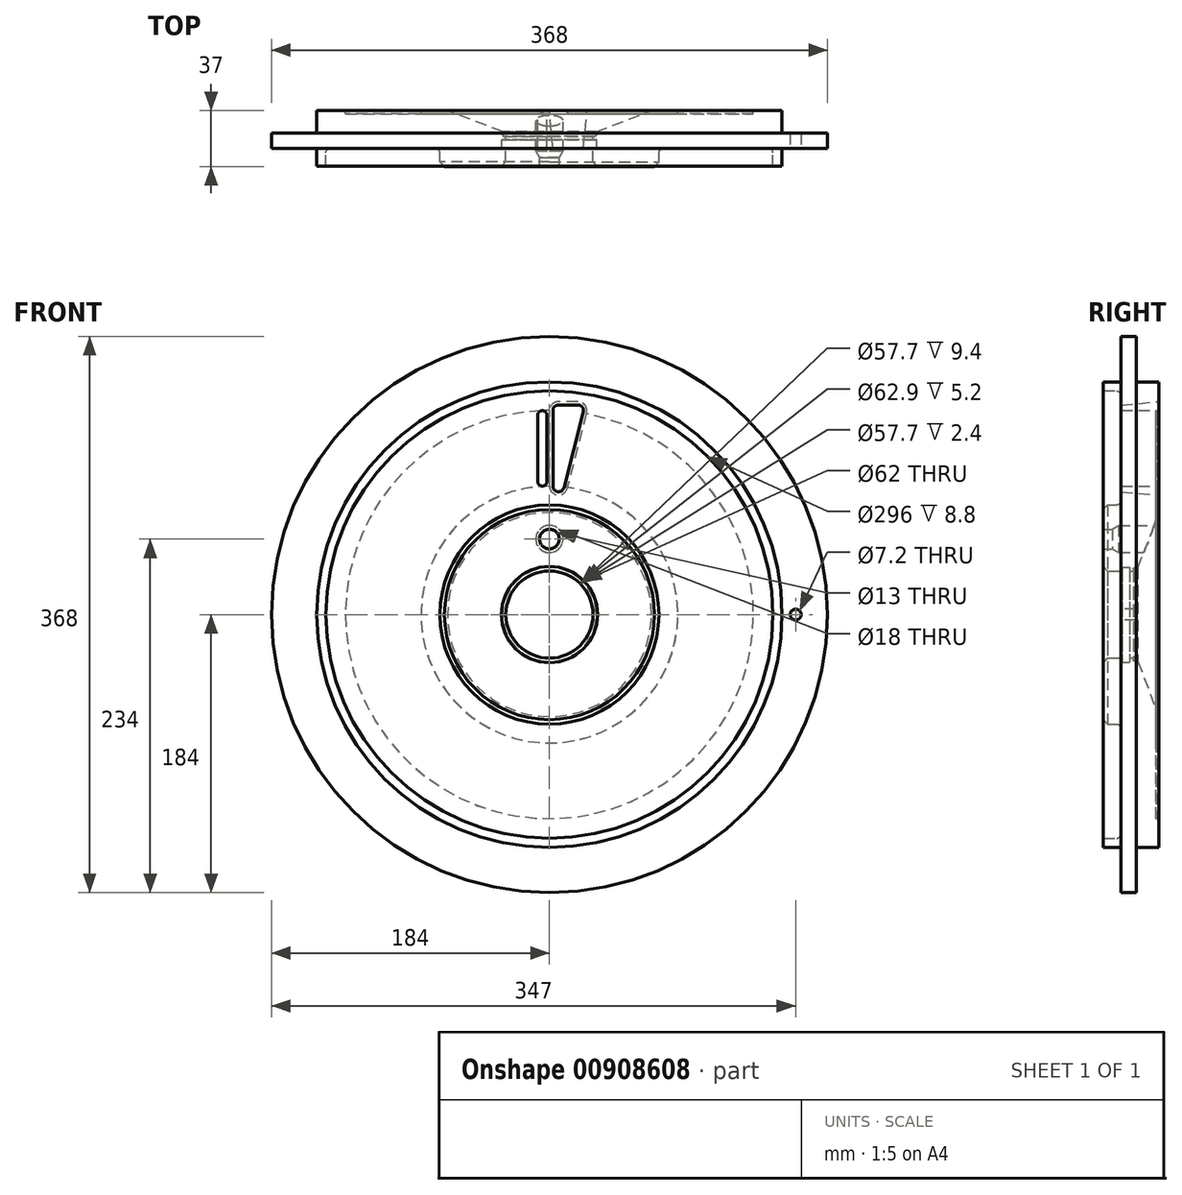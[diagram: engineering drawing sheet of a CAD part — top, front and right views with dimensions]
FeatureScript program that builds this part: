
annotation { "Feature Type Name" : "Feature", "Feature Type Description" : "" }
export const myFeature = defineFeature(function(context is Context, id is Id, definition is map)
    precondition{}
    {
        {
            var Q0;
            Q0=qCreatedBy(makeId("Top.planeOp"),FACE);
            var sketch = newSketch(context, id + "F0", { "sketchPlane" : qUnion([Q0])});
            skLineSegment(sketch, "E0", {"start": v(-72.5, 9) * mm, "end": v(-72.5, 0) * mm});
            skLineSegment(sketch, "E1", {"start": v(-72.5, 0) * mm, "end": v(-28.85, 0) * mm});
            skLineSegment(sketch, "E2", {"start": v(0, 47.35) * mm, "end": v(0, -31.33) * mm, "construction": true});
            skPoint(sketch, "E3.visualSharp", {"position": v(-72.5, 10) * mm});
            skLineSegment(sketch, "E4", {"start": v(-22.07, -0.9) * mm, "end": v(27.18, -0.9) * mm, "construction": true});
            skLineSegment(sketch, "E5", {"start": v(-154, 12) * mm, "end": v(-154, 0.2) * mm});
            skLineSegment(sketch, "E6", {"start": v(-154, 0.2) * mm, "end": v(-148, 0.2) * mm});
            skLineSegment(sketch, "E7", {"start": v(-148, 0.2) * mm, "end": v(-148, 9) * mm});
            skLineSegment(sketch, "E8", {"start": v(-28.85, 20) * mm, "end": v(-30, 20) * mm});
            skPoint(sketch, "E9.visualSharp", {"position": v(-35.7, 20) * mm});
            skLineSegment(sketch, "E10", {"start": v(-28.85, 20) * mm, "end": v(-28.85, 17.6) * mm});
            skLineSegment(sketch, "E11", {"start": v(-28.85, 17.6) * mm, "end": v(-31.45, 17.6) * mm});
            skLineSegment(sketch, "E12", {"start": v(-31.45, 17.6) * mm, "end": v(-31.45, 12.4) * mm});
            skLineSegment(sketch, "E13", {"start": v(-31.45, 12.4) * mm, "end": v(-28.85, 12.4) * mm});
            skLineSegment(sketch, "E14", {"start": v(-28.85, 12.4) * mm, "end": v(-28.85, 0) * mm});
            skLineSegment(sketch, "E15", {"start": v(-154, 12) * mm, "end": v(-184, 12) * mm});
            skLineSegment(sketch, "E16", {"start": v(-154, 37) * mm, "end": v(-67.5, 37) * mm});
            skPoint(sketch, "E17.visualSharp", {"position": v(-35, 23.4) * mm});
            skLineSegment(sketch, "E18", {"start": v(-145, 12) * mm, "end": v(-75.5, 12) * mm});
            skPoint(sketch, "E19.orphan", {"position": v(-148, 11.2) * mm});
            skPoint(sketch, "E20.visualSharp", {"position": v(-148, 12) * mm});
            skArc(sketch, "E20.filletArc", {"start": v(-145, 12) * mm, "mid": v(-147.12, 11.12) * mm, "end": v(-148, 9) * mm});
            skPoint(sketch, "E21.visualSharp", {"position": v(-72.5, 12) * mm});
            skArc(sketch, "E21.filletArc", {"start": v(-72.5, 9) * mm, "mid": v(-73.38, 11.12) * mm, "end": v(-75.5, 12) * mm});
            skLineSegment(sketch, "E22", {"start": v(-184, 12) * mm, "end": v(-184, 22) * mm});
            skLineSegment(sketch, "E23", {"start": v(-184, 22) * mm, "end": v(-154, 22) * mm});
            skLineSegment(sketch, "E24", {"start": v(-154, 22) * mm, "end": v(-154, 37) * mm});
            skLineSegment(sketch, "E25", {"start": v(-31, 23) * mm, "end": v(-67.5, 37) * mm});
            skLineSegment(sketch, "E26", {"start": v(-31, 23) * mm, "end": v(-31, 21) * mm});
            skPoint(sketch, "E27.visualSharp", {"position": v(-31, 20) * mm});
            skArc(sketch, "E27.filletArc", {"start": v(-31, 21) * mm, "mid": v(-30.7, 20.3) * mm, "end": v(-30, 20) * mm});
            skSolve(sketch);
        }
        {
            var Q0;
            Q0=makeQuery(id+"F0.imprint","IMPRINT",FACE,{"disambiguationData":[TD([[makeQuery(id+"F0.imprint","IMPRINT",EDGE,{"derivedFrom":sQuery(id+"F0.wireOp",EDGE,"E0")}),1.0]])]});
            var Q1;
            Q1=sQuery(id+"F0.wireOp",EDGE,"E2");
            revolve(context, id + "F1", {"surfaceOperationType" : NewSurfaceOperationType.NEW, "entities" : qUnion([Q0]), "axis" : qUnion([Q1]), "revolveType" : RevolveType.FULL});
        }
        {
            var Q0;
            Q0=qCreatedBy(makeId("Front.planeOp"),FACE);
            cPlane(context, id + "F2", {"entities" : qUnion([Q0]), "cplaneType" : CPlaneType.OFFSET, "offset" : 38 * mm, "oppositeDirection" : true, "width" : 150 * mm, "height" : 150 * mm});
        }
        {
            var Q0;
            Q0=qCreatedBy(id+"F2.planeOp",FACE);
            var sketch = newSketch(context, id + "F3", { "sketchPlane" : qUnion([Q0])});
            skLineSegment(sketch, "E28", {"start": v(0, 85) * mm, "end": v(0, 135) * mm});
            skLineSegment(sketch, "E29", {"start": v(6, 141) * mm, "end": v(18.84, 141) * mm});
            skLineSegment(sketch, "E30", {"start": v(24.65, 133.5) * mm, "end": v(11.81, 83.5) * mm});
            skPoint(sketch, "E31.visualSharp", {"position": v(26.57, 141) * mm});
            skArc(sketch, "E31.filletArc", {"start": v(24.65, 133.5) * mm, "mid": v(23.58, 138.68) * mm, "end": v(18.84, 141) * mm});
            skPoint(sketch, "E32.visualSharp", {"position": v(0, 37.5) * mm});
            skArc(sketch, "E32.filletArc", {"start": v(0, 85) * mm, "mid": v(5.25, 79.05) * mm, "end": v(11.81, 83.5) * mm});
            skPoint(sketch, "E33.visualSharp", {"position": v(0, 141) * mm});
            skArc(sketch, "E33.filletArc", {"start": v(6, 141) * mm, "mid": v(1.76, 139.24) * mm, "end": v(0, 135) * mm});
            skSolve(sketch);
        }
        {
            var Q0;
            Q0=qCreatedBy(makeId("Front.planeOp"),FACE);
            var sketch = newSketch(context, id + "F4", { "sketchPlane" : qUnion([Q0])});
            skCircle(sketch, "E34", {"center": v(163, 0) * mm, "radius": 3.6 * mm});
            skSolve(sketch);
        }
        {
            var Q0;
            Q0=qSketchRegion(id+"F4",true);
            extrude(context, id + "F5", {"entities" : qUnion([Q0]), "operationType" : NewBodyOperationType.REMOVE, "oppositeDirection" : true, "depth" : 50 * mm, "offsetDistance" : 25 * mm});
        }
        {
            var Q0;
            Q0=qCreatedBy(makeId("Right.planeOp"),FACE);
            var sketch = newSketch(context, id + "F6", { "sketchPlane" : qUnion([Q0])});
            skLineSegment(sketch, "E35", {"start": v(0, 50) * mm, "end": v(51.06, 50) * mm});
            skLineSegment(sketch, "E36", {"start": v(0, 56.5) * mm, "end": v(6, 56.5) * mm});
            skLineSegment(sketch, "E37", {"start": v(6, 56.5) * mm, "end": v(10.33, 59) * mm});
            skLineSegment(sketch, "E38", {"start": v(10.33, 59) * mm, "end": v(51.06, 59) * mm});
            skLineSegment(sketch, "E39", {"start": v(51.06, 59) * mm, "end": v(51.06, 50) * mm});
            skLineSegment(sketch, "E40", {"start": v(0, 50) * mm, "end": v(0, 56.5) * mm});
            skSolve(sketch);
        }
        {
            var Q0;
            Q0=qSketchRegion(id+"F6",true);
            var Q1;
            Q1=sQuery(id+"F6.wireOp",EDGE,"E35");
            revolve(context, id + "F7", {"operationType" : NewBodyOperationType.REMOVE, "surfaceOperationType" : NewSurfaceOperationType.NEW, "entities" : qUnion([Q0]), "axis" : qUnion([Q1]), "revolveType" : RevolveType.FULL, "oppositeDirection" : true});
        }
        {
            var Q0;
            Q0=makeQuery(id+"F1.opRevolve","SWEPT_EDGE",EDGE,{"disambiguationData":[OSD([sQuery(id+"F0.wireOp",EDGE,"GnCOIqdh-ukie-yiku-SOtR-T2upxGWuMmtm"),sQuery(id+"F0.wireOp",EDGE,"E1")])]});
            chamfer(context, id + "F8", {"entities" : qUnion([Q0]), "width" : 3 * mm, "tangentPropagation" : true});
        }
        {
            var Q0;
            Q0 = qSketchRegion(id + "F3", true);
            extrude(context, id + "F9", {"entities" : qUnion([Q0]), "operationType" : NewBodyOperationType.REMOVE, "depth" : 50 * mm, "offsetDistance" : 25 * mm, "hasDraft" : true, "draftAngle" : 5 * degree, "draftPullDirection" : true});
        }
        {
            var Q0;
            Q0=qCreatedBy(id+"F2.planeOp",FACE);
            var sketch = newSketch(context, id + "F10", { "sketchPlane" : qUnion([Q0])});
            skCircle(sketch, "E41", {"center": v(0, 0) * mm, "radius": 85 * mm});
            skCircle(sketch, "E42", {"center": v(0, 0) * mm, "radius": 135 * mm});
            skSolve(sketch);
        }
        {
            var Q0;
            Q0 = qSketchRegion(id + "F10", true);
            var Q1;
            Q1=makeQuery(id+"F1.opRevolve","SWEPT_FACE",FACE,{"disambiguationData":[OSD([sQuery(id+"F0.wireOp",EDGE,"E16")])]});
            extrude(context, id + "F11", {"entities" : qUnion([Q0]), "operationType" : NewBodyOperationType.REMOVE, "endBound" : BoundingType.UP_TO_SURFACE, "depth" : 25 * mm, "endBoundEntityFace" : qUnion([Q1]), "hasOffset" : true, "offsetDistance" : 2 * mm, "offsetOppositeDirection" : true});
        }
        {
            var Q0;
            Q0=qCreatedBy(id+"F2.planeOp",FACE);
            var sketch = newSketch(context, id + "F12", { "sketchPlane" : qUnion([Q0])});
            skLineSegment(sketch, "E43", {"start": v(0, 0) * mm, "end": v(0, 136.44) * mm, "construction": true});
            skLineSegment(sketch, "E44", {"start": v(-4.7, 135) * mm, "end": v(-4.7, 135) * mm});
            skLineSegment(sketch, "E45", {"start": v(-7.7, 132) * mm, "end": v(-7.7, 88) * mm});
            skLineSegment(sketch, "E46", {"start": v(-4.7, 85) * mm, "end": v(-4.7, 85) * mm});
            skLineSegment(sketch, "E47", {"start": v(-1.7, 88) * mm, "end": v(-1.7, 132) * mm});
            skPoint(sketch, "E48.visualSharp", {"position": v(-7.7, 135) * mm});
            skArc(sketch, "E48.filletArc", {"start": v(-4.7, 135) * mm, "mid": v(-6.82, 134.12) * mm, "end": v(-7.7, 132) * mm});
            skPoint(sketch, "E49.visualSharp", {"position": v(-1.7, 135) * mm});
            skArc(sketch, "E49.filletArc", {"start": v(-1.7, 132) * mm, "mid": v(-2.58, 134.12) * mm, "end": v(-4.7, 135) * mm});
            skPoint(sketch, "E50.visualSharp", {"position": v(-1.7, 85) * mm});
            skArc(sketch, "E50.filletArc", {"start": v(-4.7, 85) * mm, "mid": v(-2.58, 85.88) * mm, "end": v(-1.7, 88) * mm});
            skPoint(sketch, "E51.visualSharp", {"position": v(-7.7, 85) * mm});
            skArc(sketch, "E51.filletArc", {"start": v(-7.7, 88) * mm, "mid": v(-6.82, 85.88) * mm, "end": v(-4.7, 85) * mm});
            skSolve(sketch);
        }
        {
            var Q0;
            Q0 = qSketchRegion(id + "F12", true);
            extrude(context, id + "F13", {"entities" : qUnion([Q0]), "operationType" : NewBodyOperationType.REMOVE, "depth" : 50 * mm, "offsetDistance" : 25 * mm});
        }
    });
